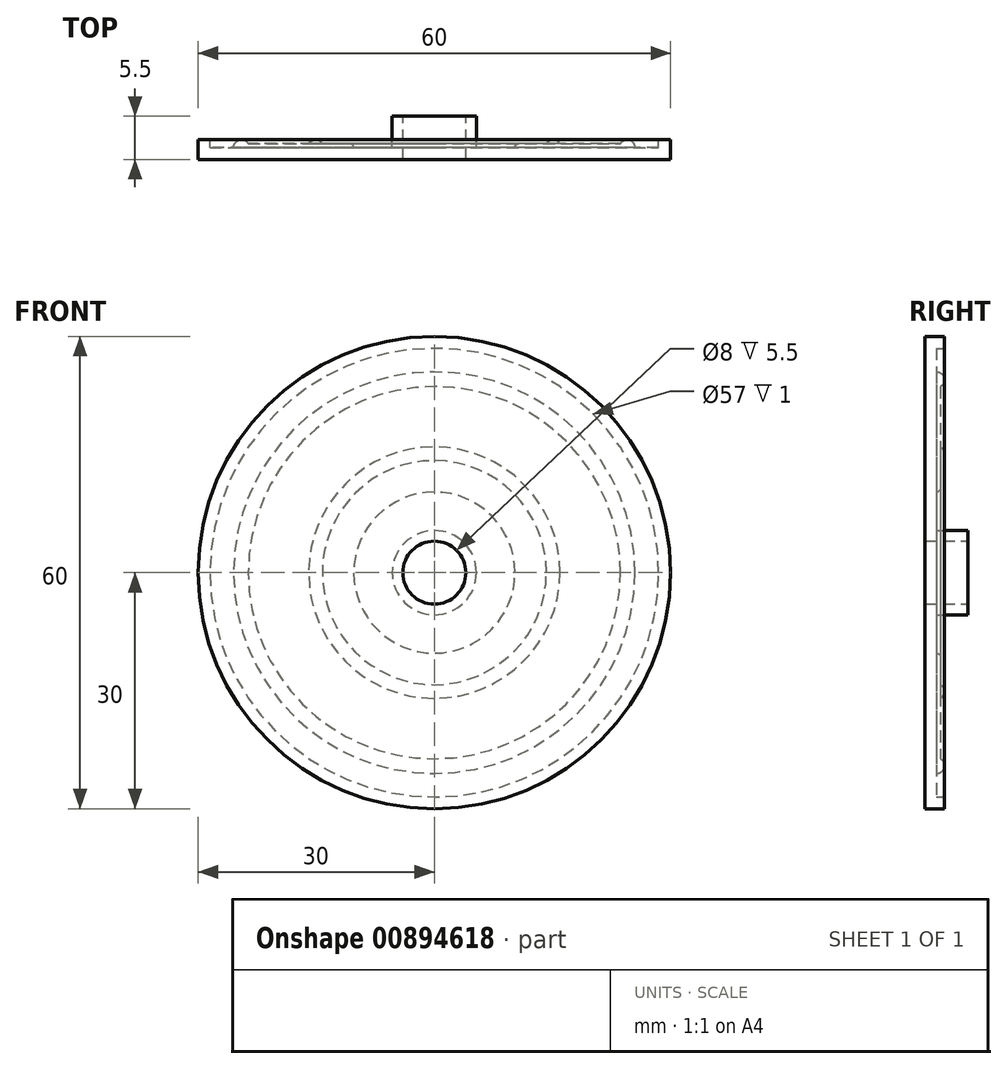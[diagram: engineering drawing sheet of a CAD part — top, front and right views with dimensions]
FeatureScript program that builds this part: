
annotation { "Feature Type Name" : "Feature", "Feature Type Description" : "" }
export const myFeature = defineFeature(function(context is Context, id is Id, definition is map)
    precondition{}
    {
        {
            var Q0;
            Q0=qCreatedBy(makeId("Top.planeOp"),FACE);
            var sketch = newSketch(context, id + "F0", { "sketchPlane" : qUnion([Q0])});
            skLineSegment(sketch, "E0", {"start": v(30, 2.5) * mm, "end": v(30, 0) * mm});
            skLineSegment(sketch, "E1", {"start": v(5.35, 1.5) * mm, "end": v(10.23, 1.5) * mm});
            skLineSegment(sketch, "E2", {"start": v(30, 2.5) * mm, "end": v(28.5, 2.5) * mm});
            skLineSegment(sketch, "E3", {"start": v(28.5, 1.5) * mm, "end": v(28.5, 2.5) * mm});
            skLineSegment(sketch, "E4", {"start": v(0, 1.5) * mm, "end": v(0, -1.5) * mm, "construction": true});
            skLineSegment(sketch, "E5", {"start": v(5.35, 1.5) * mm, "end": v(5.35, 5.5) * mm});
            skLineSegment(sketch, "E6", {"start": v(5.35, 5.5) * mm, "end": v(4, 5.5) * mm});
            skLineSegment(sketch, "E7", {"start": v(4, 5.5) * mm, "end": v(4, 1.5) * mm});
            skLineSegment(sketch, "E8", {"start": v(4, 1.5) * mm, "end": v(4, 0) * mm});
            skLineSegment(sketch, "E9.0", {"start": v(10.73, 2) * mm, "end": v(14.23, 2) * mm});
            skArc(sketch, "E10", {"start": v(25.5, 1.5) * mm, "mid": v(24.76, 2.47) * mm, "end": v(23.63, 2) * mm});
            skArc(sketch, "E11", {"start": v(10.73, 2) * mm, "mid": v(10.38, 1.85) * mm, "end": v(10.23, 1.5) * mm});
            skLineSegment(sketch, "E12.trimOffspring", {"start": v(15.97, 2) * mm, "end": v(23.63, 2) * mm});
            skArc(sketch, "E13.trimOffspring", {"start": v(15.97, 2) * mm, "mid": v(15.1, 2.5) * mm, "end": v(14.23, 2) * mm});
            skLineSegment(sketch, "E14.trimOffspring", {"start": v(25.5, 1.5) * mm, "end": v(28.5, 1.5) * mm});
            skPoint(sketch, "E15.start.orphan", {"position": v(30, -2.5) * mm});
            skPoint(sketch, "E16.end.orphan", {"position": v(5.35, -1.5) * mm});
            skPoint(sketch, "E17.end.orphan", {"position": v(5.35, -2.5) * mm});
            skPoint(sketch, "E18.orphan", {"position": v(4, -1.5) * mm});
            skLineSegment(sketch, "E19", {"start": v(4, 0) * mm, "end": v(30, 0) * mm, "construction": true});
            skLineSegment(sketch, "E20.MirrorCS", {"start": v(30, -2.5) * mm, "end": v(30, 0) * mm});
            skLineSegment(sketch, "E21.MirrorCS", {"start": v(30, -2.5) * mm, "end": v(28.5, -2.5) * mm});
            skLineSegment(sketch, "E22.MirrorCS", {"start": v(28.5, -1.5) * mm, "end": v(28.5, -2.5) * mm});
            skLineSegment(sketch, "E23.MirrorCS", {"start": v(25.5, -1.5) * mm, "end": v(28.5, -1.5) * mm});
            skArc(sketch, "E24.MirrorCS", {"start": v(25.5, -1.5) * mm, "mid": v(24.76, -2.47) * mm, "end": v(23.63, -2) * mm});
            skLineSegment(sketch, "E25.MirrorCS", {"start": v(15.97, -2) * mm, "end": v(23.63, -2) * mm});
            skArc(sketch, "E26.MirrorCS", {"start": v(15.97, -2) * mm, "mid": v(15.1, -2.5) * mm, "end": v(14.23, -2) * mm});
            skLineSegment(sketch, "E27.MirrorCS", {"start": v(10.73, -2) * mm, "end": v(14.23, -2) * mm});
            skArc(sketch, "E28.MirrorCS", {"start": v(10.73, -2) * mm, "mid": v(10.38, -1.85) * mm, "end": v(10.23, -1.5) * mm});
            skLineSegment(sketch, "E29.MirrorCS", {"start": v(5.35, -1.5) * mm, "end": v(10.23, -1.5) * mm});
            skLineSegment(sketch, "E30.MirrorCS", {"start": v(5.35, -1.5) * mm, "end": v(5.35, -2.5) * mm});
            skLineSegment(sketch, "E31.MirrorCS", {"start": v(4, -1.5) * mm, "end": v(4, 0) * mm});
            skLineSegment(sketch, "E32.MirrorCS", {"start": v(4, -2.5) * mm, "end": v(4, -1.5) * mm});
            skLineSegment(sketch, "E33", {"start": v(5.35, -2.5) * mm, "end": v(4, -2.5) * mm});
            skPoint(sketch, "E34.orphan", {"position": v(5.35, -5.5) * mm});
            skPoint(sketch, "E35.orphan", {"position": v(4, -5.5) * mm});
            skSolve(sketch);
        }
        {
            var Q0;
            Q0 = qSketchRegion(id + "F0", true);
            var Q1;
            Q1=sQuery(id+"F0.wireOp",EDGE,"E4");
            revolve(context, id + "F1", {"surfaceOperationType" : NewSurfaceOperationType.NEW, "entities" : qUnion([Q0]), "axis" : qUnion([Q1]), "revolveType" : RevolveType.FULL});
        }
        {
            var Q0;
            Q0=qCreatedBy(makeId("Top.planeOp"),FACE);
            var sketch = newSketch(context, id + "F2", { "sketchPlane" : qUnion([Q0])});
            skLineSegment(sketch, "E36", {"start": v(0, 0) * mm, "end": v(-34.88, 0) * mm});
            skLineSegment(sketch, "E37", {"start": v(-34.88, 0) * mm, "end": v(-34.88, -5.06) * mm});
            skLineSegment(sketch, "E38", {"start": v(-34.88, -5.06) * mm, "end": v(32.68, -3.5) * mm});
            skLineSegment(sketch, "E39", {"start": v(32.68, -3.5) * mm, "end": v(32.68, 0) * mm});
            skLineSegment(sketch, "E40", {"start": v(32.68, 0) * mm, "end": v(-34.88, 0) * mm});
            skSolve(sketch);
        }
        {
            var Q0;
            Q0 = qSketchRegion(id + "F2", true);
            extrude(context, id + "F3", {"entities" : qUnion([Q0]), "operationType" : NewBodyOperationType.REMOVE, "endBound" : BoundingType.SYMMETRIC, "oppositeDirection" : true, "depth" : 100 * mm, "offsetDistance" : 25 * mm});
        }
    });
